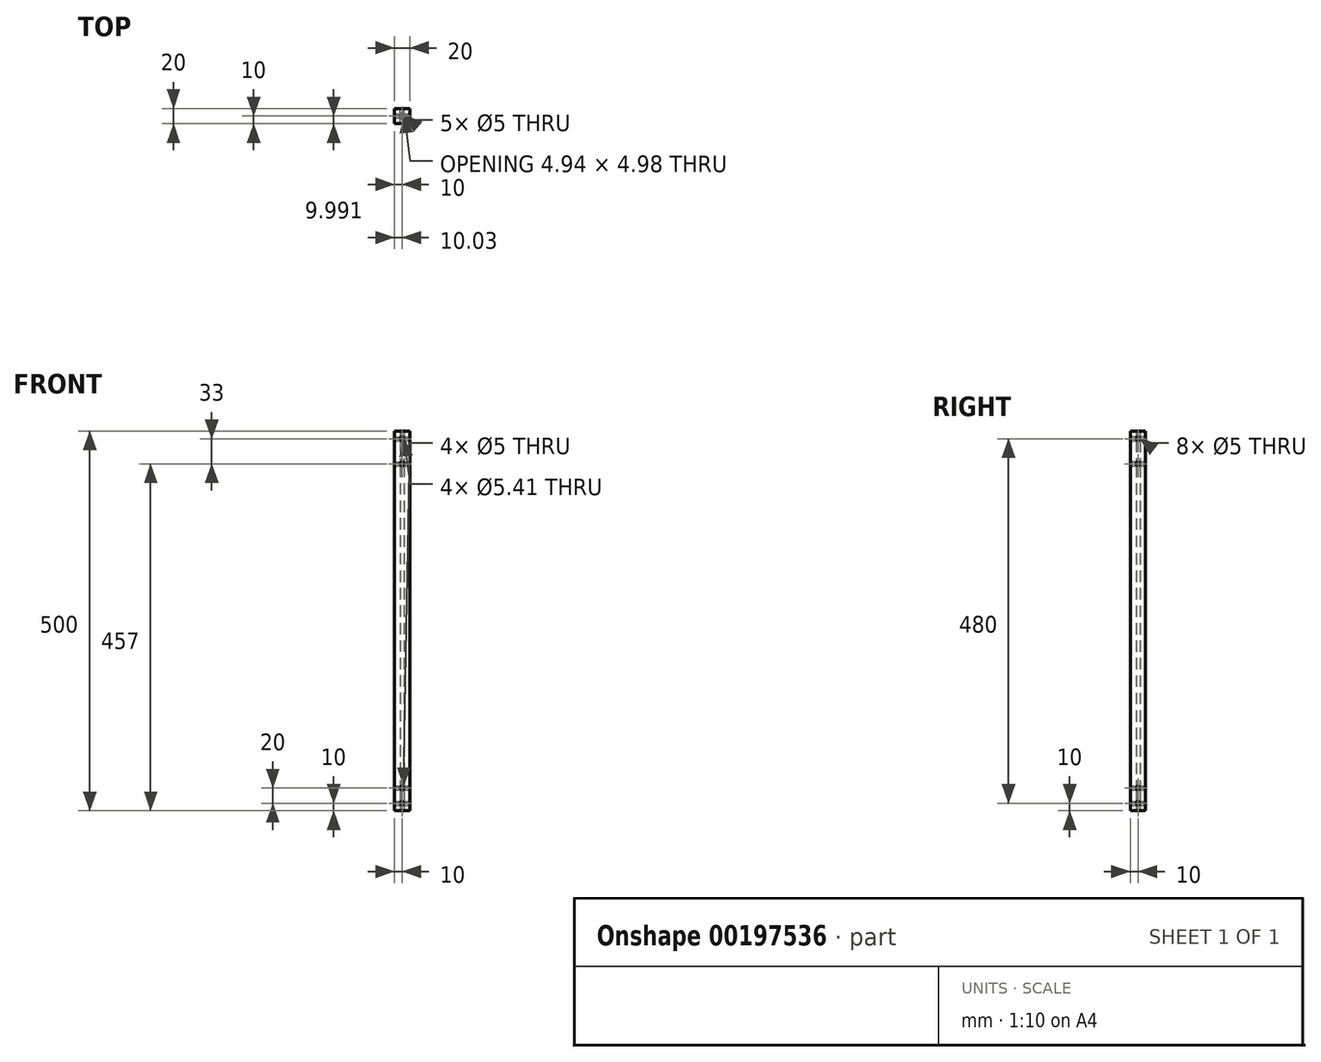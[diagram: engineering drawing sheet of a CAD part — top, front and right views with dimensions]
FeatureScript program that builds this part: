
annotation { "Feature Type Name" : "Feature", "Feature Type Description" : "" }
export const myFeature = defineFeature(function(context is Context, id is Id, definition is map)
    precondition{}
    {
        {
            var Q0;
            Q0=qCreatedBy(makeId("Top.planeOp"),FACE);
            var sketch = newSketch(context, id + "F0", { "sketchPlane" : qUnion([Q0])});
            skLineSegment(sketch, "E0.bottom", {"start": v(-10, 10) * mm, "end": v(10, 10) * mm});
            skLineSegment(sketch, "E0.top", {"start": v(-10, -10) * mm, "end": v(10, -10) * mm});
            skLineSegment(sketch, "E0.left", {"start": v(-10, 10) * mm, "end": v(-10, -10) * mm});
            skLineSegment(sketch, "E0.right", {"start": v(10, 10) * mm, "end": v(10, -10) * mm});
            skCircle(sketch, "E1", {"center": v(0, 0) * mm, "radius": 2.5 * mm});
            skSolve(sketch);
        }
        {
            var Q0;
            Q0=qSketchRegion(id+"F0",true);
            extrude(context, id + "F1", {"entities" : qUnion([Q0]), "depth" : 500 * mm});
        }
        {
            var Q0;
            Q0=makeQuery(id+"F1.opExtrude","SWEPT_FACE",FACE,{"disambiguationData":[OSD([sQuery(id+"F0.wireOp",EDGE,"E0.right")])]});
            var sketch = newSketch(context, id + "F2", { "sketchPlane" : qUnion([Q0])});
            skCircle(sketch, "E2", {"center": v(0, 10) * mm, "radius": 2.5 * mm});
            skCircle(sketch, "E3", {"center": v(0, 490) * mm, "radius": 2.5 * mm});
            skCircle(sketch, "E4", {"center": v(0, 30) * mm, "radius": 2.5 * mm});
            skCircle(sketch, "E5", {"center": v(0, 457) * mm, "radius": 2.5 * mm});
            skSolve(sketch);
        }
        {
            var Q0;
            Q0=qSketchRegion(id+"F2",true);
            extrude(context, id + "F3", {"entities" : qUnion([Q0]), "operationType" : NewBodyOperationType.REMOVE, "endBound" : BoundingType.THROUGH_ALL, "oppositeDirection" : true, "depth" : 25 * mm});
        }
        {
            var Q0;
            Q0=makeQuery(id+"F1.opExtrude","SWEPT_FACE",FACE,{"disambiguationData":[OSD([sQuery(id+"F0.wireOp",EDGE,"E0.bottom")])]});
            var sketch = newSketch(context, id + "F4", { "sketchPlane" : qUnion([Q0])});
            skCircle(sketch, "E6", {"center": v(0, 490) * mm, "radius": 2.7 * mm});
            skPoint(sketch, "E6.centerSnap0", {"position": v(0, 500) * mm});
            skCircle(sketch, "E7", {"center": v(0, 10) * mm, "radius": 2.5 * mm});
            skCircle(sketch, "E8", {"center": v(0, 457) * mm, "radius": 2.7 * mm});
            skCircle(sketch, "E9", {"center": v(0, 30) * mm, "radius": 2.5 * mm});
            skSolve(sketch);
        }
        {
            var Q0;
            Q0=qSketchRegion(id+"F4",true);
            extrude(context, id + "F5", {"entities" : qUnion([Q0]), "operationType" : NewBodyOperationType.REMOVE, "endBound" : BoundingType.THROUGH_ALL, "oppositeDirection" : true, "depth" : 25 * mm});
        }
    });
